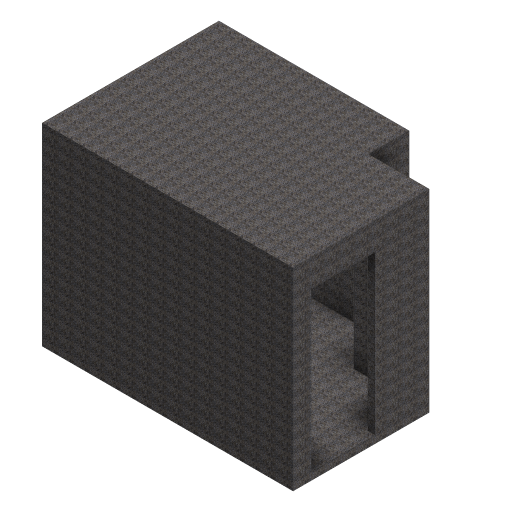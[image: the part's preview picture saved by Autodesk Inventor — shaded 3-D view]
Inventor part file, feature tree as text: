
AUTODESK INVENTOR PART (.ipt)
format: ipt  version: 2023 (Build 270158000, 158)  size: 434,176 bytes
history: native  units: mm
features: plane x11, sketch x6, extrude x5, projected_geometry x1
ambient origin geometry x8: Origin, YZ Plane, XZ Plane, XY Plane, X Axis, Y Axis, Z Axis, Center Point
bodies: 实体1 (feature_tree)
feature tree (23):
  extrude  "拉伸1"  Depth=3500.0mm
  extrude  "拉伸2"  Depth=900.0mm
  extrude  "拉伸3"  Depth=110.0mm
  extrude  "拉伸4"  Depth=110.0mm TaperAngle=0.0deg
  extrude  "拉伸5"  Depth=950.0mm
  plane  "工作平面1"
  plane  "工作平面2"
  plane  "工作平面3"
  plane  "工作平面4"
  plane  "工作平面5"
  plane  "工作平面6"
  plane  "工作平面7"
  plane  "工作平面8"
  plane  "工作平面9"
  plane  "工作平面10"
  sketch  "草图6"  dims[d13=2350.0mm d14=800.0mm d15=410.0mm d16=110.0mm d17=0.0mm d18=110.0mm d19=0.0mm d20=-110.0mm d21=-110.0mm d22=-110.0mm d23=-110.0mm d24=-110.0mm d25=-1800.0mm d26=-1500.0mm d27=-1300.0mm d28=-110.0mm d29=-110.0mm d30=0.0mm]
  plane  "工作平面11"
  sketch  "草图1"  dims[d0=2400.0mm d1=3500.0mm]
  sketch  "草图2"  dims[d2=1800.0mm d3=900.0mm]
  sketch  "草图3"  dims[d4=600.0mm d5=110.0mm]
  sketch  "草图4"  dims[d6=2650.0mm d7=0.0mm d8=110.0mm d9=0.0mm]
  sketch  "草图5"  dims[d10=110.0mm d11=0.0mm d12=950.0mm]
  projected_geometry  "投影回路1"
